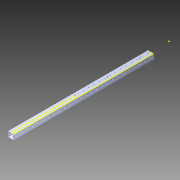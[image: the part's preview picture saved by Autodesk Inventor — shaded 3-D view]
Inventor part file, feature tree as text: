
AUTODESK INVENTOR PART (.ipt)
format: ipt  version: 2014 SP1 (Build 180222100, 222)  size: 1,289,728 bytes
history: native  units: in
note: dims shown in document units (in); Inventor stores cm internally (conversion verified against a paired STEP export)
features: sketch x2, pattern_circular x1, other x1, plane x1, extrude x1, imported_body x1
ambient origin geometry x8: Origin, YZ Plane, XZ Plane, XY Plane, X Axis, Y Axis, Z Axis, Center Point
bodies: Body1 (feature_tree)
feature tree (7):
  pattern_circular  "CirPattern2"
  other  "217-3426-STEP1"
  plane  "Work Plane1"
  extrude  "Extrusion1"  Depth=3937.0079in TaperAngle=0.0deg
  sketch  "Sketch2"
  imported_body  "Base1"
  sketch  "Sketch1"  dims[d0=-26.0in d1=3937.0079in d2=0.0in]
